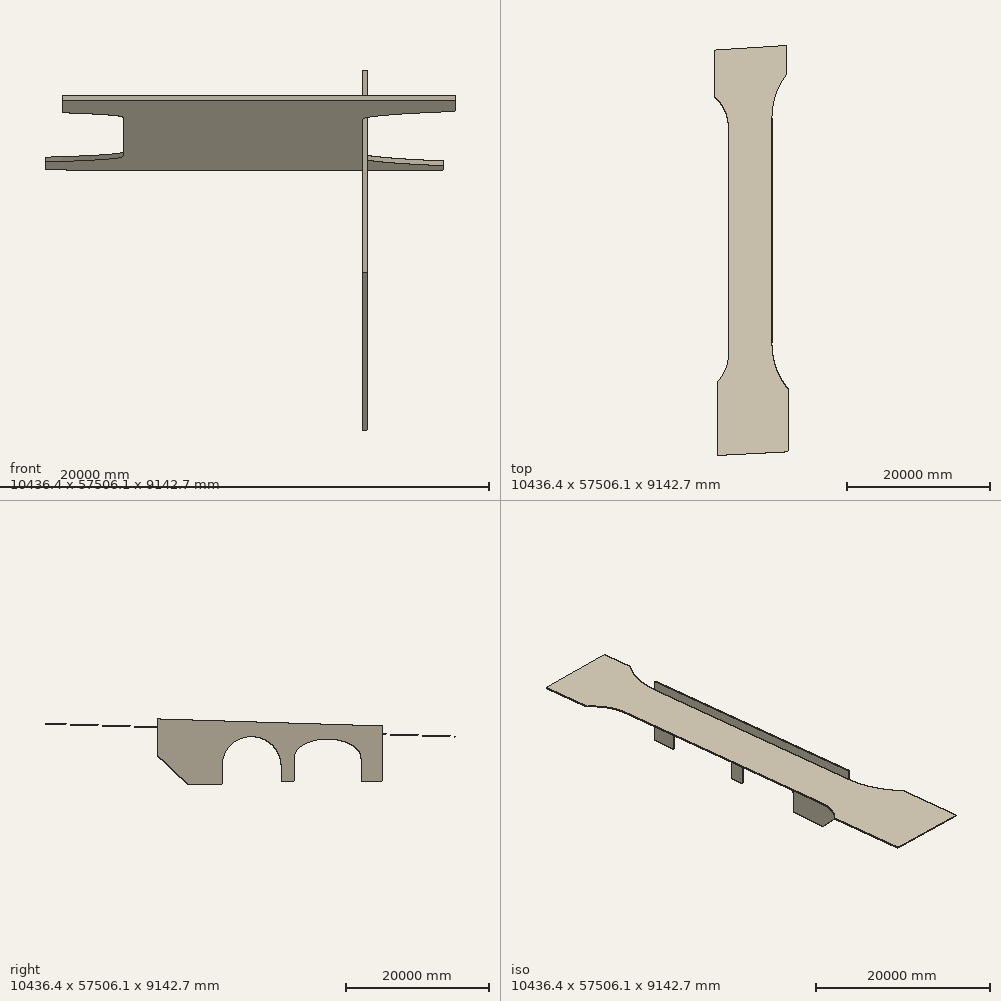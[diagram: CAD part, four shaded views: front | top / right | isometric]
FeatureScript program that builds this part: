
annotation { "Feature Type Name" : "Feature", "Feature Type Description" : "" }
export const myFeature = defineFeature(function(context is Context, id is Id, definition is map)
    precondition{}
    {
        {
            assignVariable(context, id + "F0", {"name" : "t", "anyValue" : 0.8});
        }
        {
            assignVariable(context, id + "F1", {"name" : "sc", "anyValue" : 152});
        }
        {
            var Q0;
            Q0=qCreatedBy(makeId("Right.planeOp"),FACE);
            var sketch = newSketch(context, id + "F2", { "sketchPlane" : qUnion([Q0])});
            skLineSegment(sketch, "E0", {"start": v(19469.96, 381.91) * mm, "end": v(19469.96, 3587.38) * mm});
            skArc(sketch, "E1", {"start": v(8255, 2517.64) * mm, "mid": v(4127.5, 6645.14) * mm, "end": v(0, 2517.64) * mm});
            skLineSegment(sketch, "E2", {"start": v(22517.96, 6072.14) * mm, "end": v(-9093.2, 7060.53) * mm});
            skLineSegment(sketch, "E3", {"start": v(22517.96, 7042.05) * mm, "end": v(-9093.2, 8030.44) * mm});
            skLineSegment(sketch, "E4", {"start": v(8255, 381.91) * mm, "end": v(8255, 2517.64) * mm});
            skLineSegment(sketch, "E5", {"start": v(0, 0) * mm, "end": v(0, 2517.64) * mm});
            skLineSegment(sketch, "E6", {"start": v(10093, 381.91) * mm, "end": v(10093, 3587.38) * mm});
            skLineSegment(sketch, "E7", {"start": v(22517.96, 381.91) * mm, "end": v(22517.96, 8154.31) * mm});
            skLineSegment(sketch, "E8", {"start": v(-4876.8, 0) * mm, "end": v(0, 0) * mm});
            skLineSegment(sketch, "E9", {"start": v(-9093.2, 9142.7) * mm, "end": v(22517.96, 8154.31) * mm});
            skLineSegment(sketch, "E10", {"start": v(8255, 381.91) * mm, "end": v(10093, 381.91) * mm});
            skLineSegment(sketch, "E11", {"start": v(19469.96, 381.91) * mm, "end": v(22517.96, 381.91) * mm});
            skLineSegment(sketch, "E12", {"start": v(-9093.2, 4000) * mm, "end": v(-4876.8, 0) * mm});
            skLineSegment(sketch, "E13", {"start": v(10093, 3587.38) * mm, "end": v(19469.96, 3587.38) * mm, "construction": true});
            skEllipticalArc(sketch, "E14", {});
            skLineSegment(sketch, "E15", {"start": v(-9093.2, 9142.7) * mm, "end": v(-9093.2, 4000) * mm});
            skLineSegment(sketch, "E16", {"start": v(10093, 381.91) * mm, "end": v(19469.96, 381.91) * mm, "construction": true});
            const initialGuessF2  = {"E14": [14.781480507625282, 3.587383194459892, -1, 0, 4.688480507625284, 2.722712637993906, 3.141592653589793, 0]};
            skSetInitialGuess(sketch, initialGuessF2);
            skSolve(sketch);
        }
        {
            var Q0;
            Q0 = qSketchRegion(id + "F2", true);
            extrude(context, id + "F3", {"entities" : qUnion([Q0]), "depth" : getVariable(context, 't') * getVariable(context, 'sc') * mm});
        }
        {
            var Q0;
            Q0=makeQuery(id+"F3.opExtrude","SWEPT_FACE",FACE,{"disambiguationData":[OSD([sQuery(id+"F2.wireOp",EDGE,"E9")])]});
            cPlane(context, id + "F4", {"entities" : qUnion([Q0]), "cplaneType" : CPlaneType.OFFSET, "offset" : 1112 * mm, "oppositeDirection" : true, "width" : 150 * mm, "height" : 150 * mm});
        }
        {
            var Q0;
            Q0=qCreatedBy(id+"F4.planeOp",FACE);
            var sketch = newSketch(context, id + "F5", { "sketchPlane" : qUnion([Q0])});
            skLineSegment(sketch, "E17", {"start": v(0, 22286.88) * mm, "end": v(0, -9340.6) * mm});
            skLineSegment(sketch, "E18", {"start": v(-6096, 20943.6) * mm, "end": v(-6096, -10909.75) * mm});
            skLineSegment(sketch, "E19", {"start": v(2041.34, 32494.9) * mm, "end": v(-8081.47, 31845.08) * mm});
            skLineSegment(sketch, "E20", {"start": v(-7658.77, -25035.53) * mm, "end": v(2354.92, -24519.96) * mm});
            skLineSegment(sketch, "E21", {"start": v(-8081.47, 25316.17) * mm, "end": v(-8081.47, 31845.08) * mm});
            skLineSegment(sketch, "E22", {"start": v(2041.34, 28333.56) * mm, "end": v(2041.34, 32494.9) * mm});
            skLineSegment(sketch, "E23", {"start": v(-7658.77, -14747.89) * mm, "end": v(-7658.77, -25035.53) * mm});
            skLineSegment(sketch, "E24", {"start": v(2354.92, -15830.23) * mm, "end": v(2354.92, -24519.96) * mm});
            skArc(sketch, "E25", {"start": v(-6096, 20943.6) * mm, "mid": v(-6615.61, 23344.72) * mm, "end": v(-8081.47, 25316.17) * mm});
            skArc(sketch, "E26", {"start": v(0, 22286.88) * mm, "mid": v(524.1, 25477.86) * mm, "end": v(2041.34, 28333.56) * mm});
            skArc(sketch, "E27", {"start": v(-6096, -10909.75) * mm, "mid": v(-6501.67, -12981.8) * mm, "end": v(-7658.77, -14747.89) * mm});
            skArc(sketch, "E28", {"start": v(0, -9340.6) * mm, "mid": v(606.93, -12792.44) * mm, "end": v(2354.92, -15830.23) * mm});
            skLineSegment(sketch, "E29", {"start": v(-6096, 20943.6) * mm, "end": v(0, 20943.6) * mm, "construction": true});
            skSolve(sketch);
        }
        {
            var Q0;
            Q0 = qSketchRegion(id + "F5", true);
            extrude(context, id + "F6", {"entities" : qUnion([Q0]), "operationType" : NewBodyOperationType.ADD, "oppositeDirection" : true, "depth" : getVariable(context, 't') * getVariable(context, 'sc') * mm});
        }
    });
